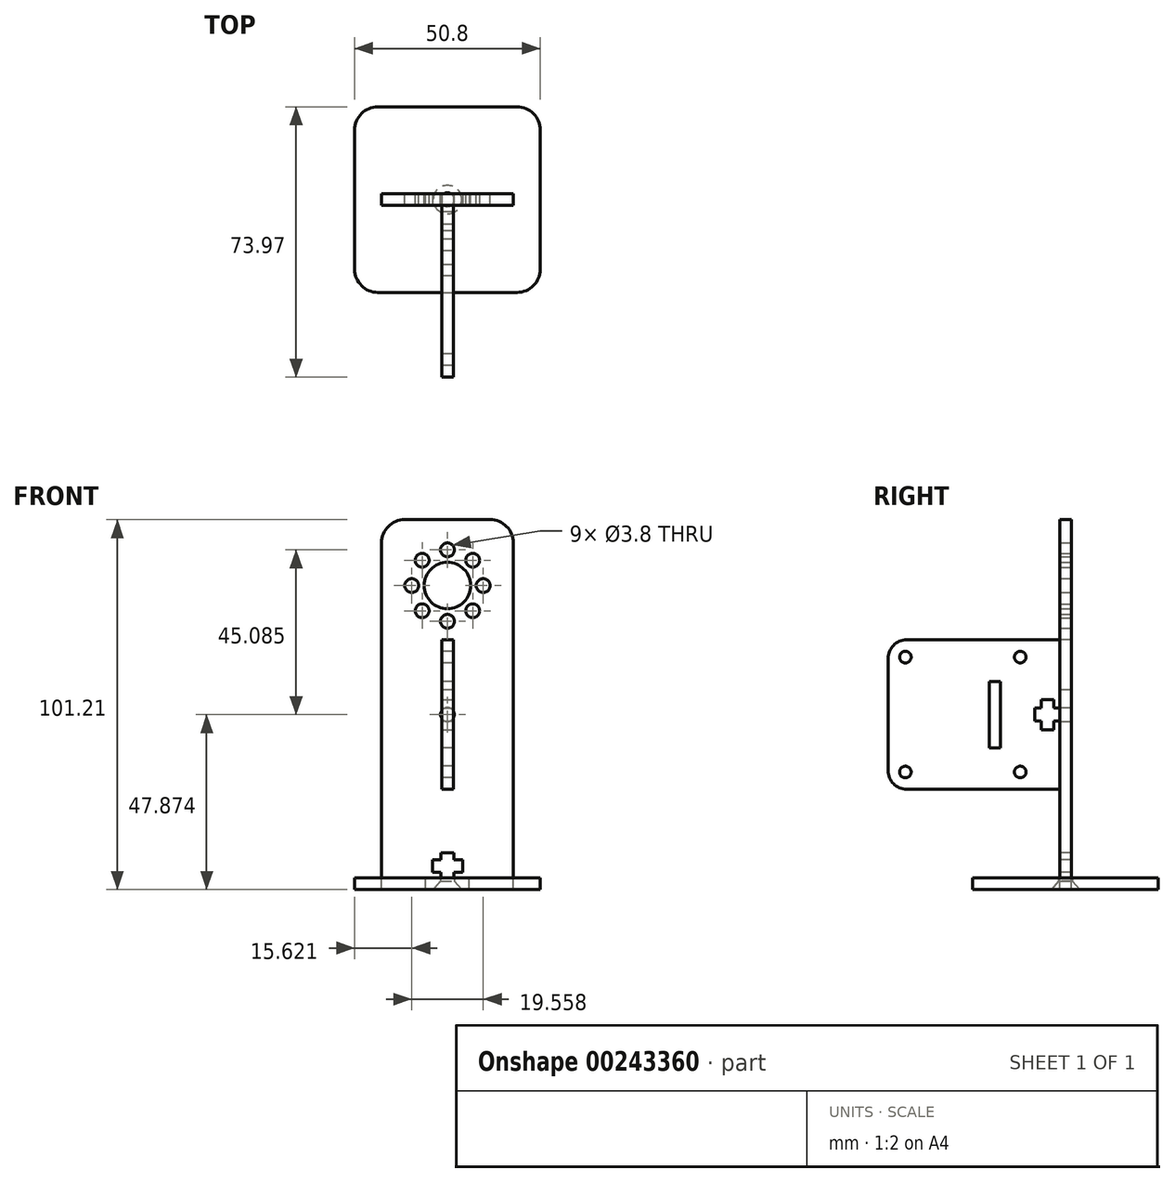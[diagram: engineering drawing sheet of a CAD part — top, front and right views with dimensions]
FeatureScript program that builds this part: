
annotation { "Feature Type Name" : "Feature", "Feature Type Description" : "" }
export const myFeature = defineFeature(function(context is Context, id is Id, definition is map)
    precondition{}
    {
        {
            var Q0;
            Q0=qCreatedBy(makeId("Front.planeOp"),FACE);
            var sketch = newSketch(context, id + "F0", { "sketchPlane" : qUnion([Q0])});
            skCircle(sketch, "E0", {"center": v(0, 0) * mm, "radius": 6.35 * mm});
            skCircle(sketch, "E1", {"center": v(0, 0) * mm, "radius": 9.78 * mm, "construction": true});
            skLineSegment(sketch, "E2", {"start": v(-6.91, 6.91) * mm, "end": v(6.91, -6.91) * mm, "construction": true});
            skLineSegment(sketch, "E3", {"start": v(-6.91, -6.91) * mm, "end": v(6.91, 6.91) * mm, "construction": true});
            skCircle(sketch, "E4", {"center": v(0, 9.78) * mm, "radius": 1.9 * mm});
            skCircle(sketch, "E5", {"center": v(6.91, 6.91) * mm, "radius": 1.9 * mm});
            skCircle(sketch, "E6", {"center": v(9.78, 0) * mm, "radius": 1.9 * mm});
            skCircle(sketch, "E7", {"center": v(6.91, -6.91) * mm, "radius": 1.9 * mm});
            skCircle(sketch, "E8", {"center": v(-6.91, -6.91) * mm, "radius": 1.9 * mm});
            skCircle(sketch, "E9", {"center": v(-6.91, 6.91) * mm, "radius": 1.9 * mm});
            skCircle(sketch, "E10", {"center": v(-9.78, 0) * mm, "radius": 1.9 * mm});
            skCircle(sketch, "E11", {"center": v(0, -9.78) * mm, "radius": 1.9 * mm});
            skLineSegment(sketch, "E12.bottom", {"start": v(-18.03, 18.03) * mm, "end": v(18.03, 18.03) * mm});
            skLineSegment(sketch, "E12.top", {"start": v(-18.03, -80) * mm, "end": v(18.03, -80) * mm});
            skLineSegment(sketch, "E12.left", {"start": v(-18.03, 18.03) * mm, "end": v(-18.03, -80) * mm});
            skLineSegment(sketch, "E12.right", {"start": v(18.03, 18.03) * mm, "end": v(18.03, -80) * mm});
            skPoint(sketch, "E13", {"position": v(0, 18.03) * mm});
            skSolve(sketch);
        }
        {
            var Q0;
            Q0 = qSketchRegion(id + "F0", true);
            extrude(context, id + "F1", {"entities" : qUnion([Q0]), "depth" : 3.17 * mm});
        }
        {
            var Q0;
            Q0=makeQuery(id+"F1.opExtrude","SWEPT_FACE",FACE,{"disambiguationData":[OSD([sQuery(id+"F0.wireOp",EDGE,"E12.top")])]});
            var sketch = newSketch(context, id + "F2", { "sketchPlane" : qUnion([Q0])});
            skLineSegment(sketch, "E14", {"start": v(-18.03, 3.18) * mm, "end": v(18.03, 0) * mm, "construction": true});
            skLineSegment(sketch, "E15.bottom", {"start": v(-25.4, 26.99) * mm, "end": v(25.4, 26.99) * mm});
            skLineSegment(sketch, "E15.top", {"start": v(-25.4, -23.81) * mm, "end": v(25.4, -23.81) * mm});
            skLineSegment(sketch, "E15.left", {"start": v(-25.4, 26.99) * mm, "end": v(-25.4, -23.81) * mm});
            skLineSegment(sketch, "E15.right", {"start": v(25.4, 26.99) * mm, "end": v(25.4, -23.81) * mm});
            skPoint(sketch, "E15.middle", {"position": v(0, 1.59) * mm});
            skSolve(sketch);
        }
        {
            var Q0;
            Q0 = qSketchRegion(id + "F2", true);
            extrude(context, id + "F3", {"entities" : qUnion([Q0]), "depth" : 3.17 * mm});
        }
        {
            var Q0;
            Q0=makeQuery(id+"F1.opExtrude","SWEPT_FACE",FACE,{"disambiguationData":[OSD([sQuery(id+"F0.wireOp",EDGE,"E12.top")])]});
            var sketch = newSketch(context, id + "F4", { "sketchPlane" : qUnion([Q0])});
            skLineSegment(sketch, "E16.bottom", {"start": v(-18.03, 3.18) * mm, "end": v(-6, 3.18) * mm});
            skLineSegment(sketch, "E16.top", {"start": v(-18.03, 0) * mm, "end": v(-6, 0) * mm});
            skLineSegment(sketch, "E16.left", {"start": v(-18.03, 3.18) * mm, "end": v(-18.03, 0) * mm});
            skLineSegment(sketch, "E16.right", {"start": v(-6, 3.18) * mm, "end": v(-6, 0) * mm});
            skLineSegment(sketch, "E17.bottom", {"start": v(-6, 0) * mm, "end": v(6, 0) * mm});
            skLineSegment(sketch, "E17.top", {"start": v(-6, 3.18) * mm, "end": v(6, 3.18) * mm});
            skLineSegment(sketch, "E17.left", {"start": v(-6, 0) * mm, "end": v(-6, 3.18) * mm});
            skLineSegment(sketch, "E17.right", {"start": v(6, 0) * mm, "end": v(6, 3.18) * mm});
            skLineSegment(sketch, "E18.bottom", {"start": v(6, 3.18) * mm, "end": v(18.03, 3.18) * mm});
            skLineSegment(sketch, "E18.top", {"start": v(6, 0) * mm, "end": v(18.03, 0) * mm});
            skLineSegment(sketch, "E18.left", {"start": v(6, 3.18) * mm, "end": v(6, 0) * mm});
            skLineSegment(sketch, "E18.right", {"start": v(18.03, 3.18) * mm, "end": v(18.03, 0) * mm});
            skSolve(sketch);
        }
        {
            var Q0;
            Q0=makeQuery(id+"F4.imprint","IMPRINT",FACE,{"disambiguationData":[TD([[makeQuery(id+"F4.imprint","IMPRINT",EDGE,{"derivedFrom":sQuery(id+"F4.wireOp",EDGE,"E16.bottom")}),-1.0]])]});
            var Q1;
            Q1=makeQuery(id+"F4.imprint","IMPRINT",FACE,{"disambiguationData":[TD([[makeQuery(id+"F4.imprint","IMPRINT",EDGE,{"derivedFrom":sQuery(id+"F4.wireOp",EDGE,"E18.bottom")}),-1.0]])]});
            extrude(context, id + "F5", {"entities" : qUnion([Q0, Q1]), "depth" : 3.17 * mm});
        }
        {
            var Q0;
            Q0=makeQuery(id+"F5.opExtrude","SWEPT_BODY",BODY,{"disambiguationData":[OSD([sQuery(id+"F4.wireOp",EDGE,"E18.bottom"),sQuery(id+"F4.wireOp",EDGE,"E18.top"),sQuery(id+"F4.wireOp",EDGE,"E18.left"),sQuery(id+"F4.wireOp",EDGE,"E18.right")])]});
            var Q1;
            Q1=makeQuery(id+"F5.opExtrude","SWEPT_BODY",BODY,{"disambiguationData":[OSD([sQuery(id+"F4.wireOp",EDGE,"E16.bottom"),sQuery(id+"F4.wireOp",EDGE,"E16.top"),sQuery(id+"F4.wireOp",EDGE,"E16.left"),sQuery(id+"F4.wireOp",EDGE,"E17.left")])]});
            var Q2;
            Q2=makeQuery(id+"F3.opExtrude","SWEPT_BODY",BODY,{"disambiguationData":[OSD([sQuery(id+"F2.wireOp",EDGE,"E15.bottom"),sQuery(id+"F2.wireOp",EDGE,"E15.top"),sQuery(id+"F2.wireOp",EDGE,"E15.left"),sQuery(id+"F2.wireOp",EDGE,"E15.right")])]});
            booleanBodies(context, id + "F6", {"operationType" : BooleanOperationType.SUBTRACTION, "tools" : qUnion([Q0, Q1]), "targets" : qUnion([Q2]), "keepTools" : true});
        }
        {
            var Q0;
            Q0=makeQuery(id+"F5.opExtrude","SWEPT_BODY",BODY,{"disambiguationData":[OSD([sQuery(id+"F4.wireOp",EDGE,"E16.bottom"),sQuery(id+"F4.wireOp",EDGE,"E16.top"),sQuery(id+"F4.wireOp",EDGE,"E16.left"),sQuery(id+"F4.wireOp",EDGE,"E17.left")])]});
            var Q1;
            Q1=makeQuery(id+"F5.opExtrude","SWEPT_BODY",BODY,{"disambiguationData":[OSD([sQuery(id+"F4.wireOp",EDGE,"E18.bottom"),sQuery(id+"F4.wireOp",EDGE,"E18.top"),sQuery(id+"F4.wireOp",EDGE,"E18.left"),sQuery(id+"F4.wireOp",EDGE,"E18.right")])]});
            var Q2;
            Q2=makeQuery(id+"F1.opExtrude","SWEPT_BODY",BODY,{"disambiguationData":[OSD([sQuery(id+"F0.wireOp",EDGE,"E0"),sQuery(id+"F0.wireOp",EDGE,"E4"),sQuery(id+"F0.wireOp",EDGE,"E5"),sQuery(id+"F0.wireOp",EDGE,"E6"),sQuery(id+"F0.wireOp",EDGE,"E7"),sQuery(id+"F0.wireOp",EDGE,"E8"),sQuery(id+"F0.wireOp",EDGE,"E9"),sQuery(id+"F0.wireOp",EDGE,"E10"),sQuery(id+"F0.wireOp",EDGE,"E11"),sQuery(id+"F0.wireOp",EDGE,"E12.bottom"),sQuery(id+"F0.wireOp",EDGE,"E12.top"),sQuery(id+"F0.wireOp",EDGE,"E12.left"),sQuery(id+"F0.wireOp",EDGE,"E12.right")])]});
            booleanBodies(context, id + "F7", {"operationType" : BooleanOperationType.UNION, "tools" : qUnion([Q0, Q1, Q2])});
        }
        {
            var Q0;
            Q0=makeQuery(id+"F3.opExtrude","CAP_FACE",FACE,{"disambiguationData":[OSD([sQuery(id+"F2.wireOp",EDGE,"E15.bottom"),sQuery(id+"F2.wireOp",EDGE,"E15.top"),sQuery(id+"F2.wireOp",EDGE,"E15.left"),sQuery(id+"F2.wireOp",EDGE,"E15.right")])],"isStart":false});
            var sketch = newSketch(context, id + "F8", { "sketchPlane" : qUnion([Q0])});
            skLineSegment(sketch, "E19", {"start": v(-6, 3.17) * mm, "end": v(6, 0) * mm, "construction": true});
            skCircle(sketch, "E20", {"center": v(0, 1.59) * mm, "radius": 1.9 * mm});
            skSolve(sketch);
        }
        {
            var Q0;
            Q0 = qSketchRegion(id + "F8", true);
            var Q1;
            Q1=makeQuery(id+"F3.opExtrude","CAP_FACE",FACE,{"disambiguationData":[OSD([sQuery(id+"F2.wireOp",EDGE,"E15.bottom"),sQuery(id+"F2.wireOp",EDGE,"E15.top"),sQuery(id+"F2.wireOp",EDGE,"E15.left"),sQuery(id+"F2.wireOp",EDGE,"E15.right")])],"isStart":true});
            extrude(context, id + "F9", {"entities" : qUnion([Q0]), "operationType" : NewBodyOperationType.REMOVE, "endBound" : BoundingType.UP_TO_SURFACE, "oppositeDirection" : true, "endBoundEntityFace" : qUnion([Q1]), "depth" : 25.4 * mm});
        }
        {
            var Q0;
            Q0=makeQuery(id+"F7.opBoolean","MERGE",FACE,{"derivedFrom":[makeQuery(id+"F1.opExtrude","CAP_FACE",FACE,{"disambiguationData":[OSD([sQuery(id+"F0.wireOp",EDGE,"E0"),sQuery(id+"F0.wireOp",EDGE,"E4"),sQuery(id+"F0.wireOp",EDGE,"E5"),sQuery(id+"F0.wireOp",EDGE,"E6"),sQuery(id+"F0.wireOp",EDGE,"E7"),sQuery(id+"F0.wireOp",EDGE,"E8"),sQuery(id+"F0.wireOp",EDGE,"E9"),sQuery(id+"F0.wireOp",EDGE,"E10"),sQuery(id+"F0.wireOp",EDGE,"E11"),sQuery(id+"F0.wireOp",EDGE,"E12.bottom"),sQuery(id+"F0.wireOp",EDGE,"E12.top"),sQuery(id+"F0.wireOp",EDGE,"E12.left"),sQuery(id+"F0.wireOp",EDGE,"E12.right")])],"isStart":false}),makeQuery(id+"F5.opExtrude","SWEPT_FACE",FACE,{"disambiguationData":[OSD([sQuery(id+"F4.wireOp",EDGE,"E16.bottom")])]}),makeQuery(id+"F5.opExtrude","SWEPT_FACE",FACE,{"disambiguationData":[OSD([sQuery(id+"F4.wireOp",EDGE,"E18.bottom")])]})]});
            var sketch = newSketch(context, id + "F10", { "sketchPlane" : qUnion([Q0])});
            skLineSegment(sketch, "E21", {"start": v(0, -80) * mm, "end": v(0, -73.14) * mm, "construction": true});
            skPoint(sketch, "E21.endSnap0", {"position": v(0, -80) * mm});
            skLineSegment(sketch, "E22", {"start": v(0, -73.14) * mm, "end": v(-1.78, -73.14) * mm});
            skLineSegment(sketch, "E23", {"start": v(-1.78, -73.14) * mm, "end": v(-1.78, -74.97) * mm});
            skLineSegment(sketch, "E24", {"start": v(-1.78, -74.97) * mm, "end": v(-4.13, -74.97) * mm});
            skLineSegment(sketch, "E25", {"start": v(-4.13, -74.97) * mm, "end": v(-4.13, -78.4) * mm});
            skLineSegment(sketch, "E26", {"start": v(-4.13, -78.4) * mm, "end": v(-1.78, -78.4) * mm});
            skLineSegment(sketch, "E27", {"start": v(-1.78, -78.4) * mm, "end": v(-1.78, -80) * mm});
            skLineSegment(sketch, "E28", {"start": v(-1.78, -80) * mm, "end": v(0, -80) * mm});
            skLineSegment(sketch, "E29.MirrorCS", {"start": v(0, -73.14) * mm, "end": v(1.78, -73.14) * mm});
            skLineSegment(sketch, "E30.MirrorCS", {"start": v(1.78, -73.14) * mm, "end": v(1.78, -74.97) * mm});
            skLineSegment(sketch, "E31.MirrorCS", {"start": v(1.78, -74.97) * mm, "end": v(4.13, -74.97) * mm});
            skLineSegment(sketch, "E32.MirrorCS", {"start": v(4.13, -74.97) * mm, "end": v(4.13, -78.4) * mm});
            skLineSegment(sketch, "E33.MirrorCS", {"start": v(4.13, -78.4) * mm, "end": v(1.78, -78.4) * mm});
            skLineSegment(sketch, "E34.MirrorCS", {"start": v(1.78, -78.4) * mm, "end": v(1.78, -80) * mm});
            skLineSegment(sketch, "E35.MirrorCS", {"start": v(1.78, -80) * mm, "end": v(0, -80) * mm});
            skSolve(sketch);
        }
        {
            var Q0;
            Q0 = qSketchRegion(id + "F10", true);
            var Q1;
            Q1=makeQuery(id+"F7.opBoolean","MERGE",FACE,{"derivedFrom":[makeQuery(id+"F1.opExtrude","CAP_FACE",FACE,{"disambiguationData":[OSD([sQuery(id+"F0.wireOp",EDGE,"E0"),sQuery(id+"F0.wireOp",EDGE,"E4"),sQuery(id+"F0.wireOp",EDGE,"E5"),sQuery(id+"F0.wireOp",EDGE,"E6"),sQuery(id+"F0.wireOp",EDGE,"E7"),sQuery(id+"F0.wireOp",EDGE,"E8"),sQuery(id+"F0.wireOp",EDGE,"E9"),sQuery(id+"F0.wireOp",EDGE,"E10"),sQuery(id+"F0.wireOp",EDGE,"E11"),sQuery(id+"F0.wireOp",EDGE,"E12.bottom"),sQuery(id+"F0.wireOp",EDGE,"E12.top"),sQuery(id+"F0.wireOp",EDGE,"E12.left"),sQuery(id+"F0.wireOp",EDGE,"E12.right")])],"isStart":true}),makeQuery(id+"F5.opExtrude","SWEPT_FACE",FACE,{"disambiguationData":[OSD([sQuery(id+"F4.wireOp",EDGE,"E16.top")])]}),makeQuery(id+"F5.opExtrude","SWEPT_FACE",FACE,{"disambiguationData":[OSD([sQuery(id+"F4.wireOp",EDGE,"E18.top")])]})]});
            extrude(context, id + "F11", {"entities" : qUnion([Q0]), "operationType" : NewBodyOperationType.REMOVE, "endBound" : BoundingType.UP_TO_SURFACE, "oppositeDirection" : true, "endBoundEntityFace" : qUnion([Q1]), "depth" : 25.4 * mm});
        }
        {
            var Q0;
            Q0=sQuery(id+"F8.wireOp",VERTEX,"E20.center");
            var Q1;
            Q1=makeQuery(id+"F3.opExtrude","SWEPT_BODY",BODY,{"disambiguationData":[OSD([sQuery(id+"F2.wireOp",EDGE,"E15.bottom"),sQuery(id+"F2.wireOp",EDGE,"E15.top"),sQuery(id+"F2.wireOp",EDGE,"E15.left"),sQuery(id+"F2.wireOp",EDGE,"E15.right")])]});
            hole(context, id + "F12", {"style" : HoleStyle.C_SINK, "endStyle" : HoleEndStyle.THROUGH, "holeDiameter" : 3.8 * mm, "cSinkDiameter" : 7.8 * mm, "cSinkAngle" : 82 * degree, "tappedDepth" : 12.7 * mm, "tapClearance" : 3, "locations" : qUnion([Q0]), "scope" : qUnion([Q1])});
        }
        {
            var Q0;
            Q0=makeQuery(id+"F3.opExtrude","SWEPT_EDGE",EDGE,{"disambiguationData":[OSD([sQuery(id+"F2.wireOp",EDGE,"E15.bottom"),sQuery(id+"F2.wireOp",EDGE,"E15.left")])]});
            var Q1;
            Q1=makeQuery(id+"F3.opExtrude","SWEPT_EDGE",EDGE,{"disambiguationData":[OSD([sQuery(id+"F2.wireOp",EDGE,"E15.top"),sQuery(id+"F2.wireOp",EDGE,"E15.left")])]});
            var Q2;
            Q2=makeQuery(id+"F3.opExtrude","SWEPT_EDGE",EDGE,{"disambiguationData":[OSD([sQuery(id+"F2.wireOp",EDGE,"E15.top"),sQuery(id+"F2.wireOp",EDGE,"E15.right")])]});
            var Q3;
            Q3=makeQuery(id+"F3.opExtrude","SWEPT_EDGE",EDGE,{"disambiguationData":[OSD([sQuery(id+"F2.wireOp",EDGE,"E15.bottom"),sQuery(id+"F2.wireOp",EDGE,"E15.right")])]});
            var Q4;
            Q4=makeQuery(id+"F1.opExtrude","SWEPT_EDGE",EDGE,{"disambiguationData":[OSD([sQuery(id+"F0.wireOp",EDGE,"E12.bottom"),sQuery(id+"F0.wireOp",EDGE,"E12.right")])]});
            var Q5;
            Q5=makeQuery(id+"F1.opExtrude","SWEPT_EDGE",EDGE,{"disambiguationData":[OSD([sQuery(id+"F0.wireOp",EDGE,"E12.bottom"),sQuery(id+"F0.wireOp",EDGE,"E12.left")])]});
            fillet(context, id + "F13", {"entities" : qUnion([Q0, Q1, Q2, Q3, Q4, Q5]), "radius" : 6.35 * mm, "tangentPropagation" : true, "allowEdgeOverflow" : false});
        }
        {
            var Q0;
            Q0=makeQuery(id+"F7.opBoolean","MERGE",FACE,{"derivedFrom":[makeQuery(id+"F1.opExtrude","CAP_FACE",FACE,{"disambiguationData":[OSD([sQuery(id+"F0.wireOp",EDGE,"E0"),sQuery(id+"F0.wireOp",EDGE,"E4"),sQuery(id+"F0.wireOp",EDGE,"E5"),sQuery(id+"F0.wireOp",EDGE,"E6"),sQuery(id+"F0.wireOp",EDGE,"E7"),sQuery(id+"F0.wireOp",EDGE,"E8"),sQuery(id+"F0.wireOp",EDGE,"E9"),sQuery(id+"F0.wireOp",EDGE,"E10"),sQuery(id+"F0.wireOp",EDGE,"E11"),sQuery(id+"F0.wireOp",EDGE,"E12.bottom"),sQuery(id+"F0.wireOp",EDGE,"E12.top"),sQuery(id+"F0.wireOp",EDGE,"E12.left"),sQuery(id+"F0.wireOp",EDGE,"E12.right")])],"isStart":false}),makeQuery(id+"F5.opExtrude","SWEPT_FACE",FACE,{"disambiguationData":[OSD([sQuery(id+"F4.wireOp",EDGE,"E16.bottom")])]}),makeQuery(id+"F5.opExtrude","SWEPT_FACE",FACE,{"disambiguationData":[OSD([sQuery(id+"F4.wireOp",EDGE,"E18.bottom")])]})]});
            var sketch = newSketch(context, id + "F14", { "sketchPlane" : qUnion([Q0])});
            skLineSegment(sketch, "E36.bottom", {"start": v(1.59, -55.76) * mm, "end": v(-1.59, -55.76) * mm});
            skLineSegment(sketch, "E36.top", {"start": v(1.59, -14.85) * mm, "end": v(-1.59, -14.85) * mm});
            skLineSegment(sketch, "E36.left", {"start": v(1.59, -55.76) * mm, "end": v(1.59, -14.85) * mm});
            skLineSegment(sketch, "E36.right", {"start": v(-1.59, -55.76) * mm, "end": v(-1.59, -14.85) * mm});
            skPoint(sketch, "E36.middle", {"position": v(0, -35.3) * mm});
            skSolve(sketch);
        }
        {
            var Q0;
            Q0 = qSketchRegion(id + "F14", true);
            extrude(context, id + "F15", {"entities" : qUnion([Q0]), "depth" : 47 * mm});
        }
        {
            var Q0;
            Q0=makeQuery(id+"F15.opExtrude","SWEPT_FACE",FACE,{"disambiguationData":[OSD([sQuery(id+"F14.wireOp",EDGE,"E36.right")])]});
            var sketch = newSketch(context, id + "F16", { "sketchPlane" : qUnion([Q0])});
            skCircle(sketch, "E37", {"center": v(14, -19.59) * mm, "radius": 1.59 * mm});
            skCircle(sketch, "E38", {"center": v(14, -51.02) * mm, "radius": 1.59 * mm});
            skCircle(sketch, "E39", {"center": v(45.43, -51.02) * mm, "radius": 1.59 * mm});
            skCircle(sketch, "E40", {"center": v(45.43, -19.59) * mm, "radius": 1.59 * mm});
            skLineSegment(sketch, "E41", {"start": v(3.18, -35.3) * mm, "end": v(50.16, -35.3) * mm, "construction": true});
            skLineSegment(sketch, "E42", {"start": v(45.43, -19.59) * mm, "end": v(45.43, -51.02) * mm, "construction": true});
            skPoint(sketch, "E43", {"position": v(45.43, -35.3) * mm});
            skLineSegment(sketch, "E44", {"start": v(45.43, -19.59) * mm, "end": v(14, -19.59) * mm, "construction": true});
            skLineSegment(sketch, "E45.bottom", {"start": v(22.48, -26.21) * mm, "end": v(19.43, -26.21) * mm});
            skLineSegment(sketch, "E45.top", {"start": v(22.48, -44.4) * mm, "end": v(19.43, -44.4) * mm});
            skLineSegment(sketch, "E45.left", {"start": v(22.48, -26.21) * mm, "end": v(22.48, -44.4) * mm});
            skLineSegment(sketch, "E45.right", {"start": v(19.43, -26.21) * mm, "end": v(19.43, -44.4) * mm});
            skPoint(sketch, "E45.middle", {"position": v(20.95, -35.3) * mm});
            skLineSegment(sketch, "E46", {"start": v(45.43, -19.59) * mm, "end": v(45.43, -14.85) * mm, "construction": true});
            skLineSegment(sketch, "E47", {"start": v(45.43, -19.59) * mm, "end": v(50.16, -19.59) * mm, "construction": true});
            skSolve(sketch);
        }
        {
            var Q0;
            Q0 = qSketchRegion(id + "F16", true);
            var Q1;
            Q1=makeQuery(id+"F15.opExtrude","SWEPT_FACE",FACE,{"disambiguationData":[OSD([sQuery(id+"F14.wireOp",EDGE,"E36.left")])]});
            extrude(context, id + "F17", {"entities" : qUnion([Q0]), "operationType" : NewBodyOperationType.REMOVE, "endBound" : BoundingType.UP_TO_SURFACE, "oppositeDirection" : true, "endBoundEntityFace" : qUnion([Q1]), "depth" : 25.4 * mm});
        }
        {
            var Q0;
            Q0=makeQuery(id+"F15.opExtrude","CAP_FACE",FACE,{"disambiguationData":[OSD([sQuery(id+"F14.wireOp",EDGE,"E36.bottom"),sQuery(id+"F14.wireOp",EDGE,"E36.top"),sQuery(id+"F14.wireOp",EDGE,"E36.left"),sQuery(id+"F14.wireOp",EDGE,"E36.right")])],"isStart":true});
            var sketch = newSketch(context, id + "F18", { "sketchPlane" : qUnion([Q0])});
            skLineSegment(sketch, "E48.bottom", {"start": v(-1.59, -14.85) * mm, "end": v(1.59, -14.85) * mm});
            skLineSegment(sketch, "E48.top", {"start": v(-1.59, -28.49) * mm, "end": v(1.59, -28.49) * mm});
            skLineSegment(sketch, "E48.left", {"start": v(-1.59, -14.85) * mm, "end": v(-1.59, -28.49) * mm});
            skLineSegment(sketch, "E48.right", {"start": v(1.59, -14.85) * mm, "end": v(1.59, -28.49) * mm});
            skLineSegment(sketch, "E49.bottom", {"start": v(1.59, -28.49) * mm, "end": v(-1.59, -28.49) * mm});
            skLineSegment(sketch, "E49.top", {"start": v(1.59, -42.12) * mm, "end": v(-1.59, -42.12) * mm});
            skLineSegment(sketch, "E49.left", {"start": v(1.59, -28.49) * mm, "end": v(1.59, -42.12) * mm});
            skLineSegment(sketch, "E49.right", {"start": v(-1.59, -28.49) * mm, "end": v(-1.59, -42.12) * mm});
            skLineSegment(sketch, "E50.bottom", {"start": v(-1.59, -42.12) * mm, "end": v(1.59, -42.12) * mm});
            skLineSegment(sketch, "E50.top", {"start": v(-1.59, -55.76) * mm, "end": v(1.59, -55.76) * mm});
            skLineSegment(sketch, "E50.left", {"start": v(-1.59, -42.12) * mm, "end": v(-1.59, -55.76) * mm});
            skLineSegment(sketch, "E50.right", {"start": v(1.59, -42.12) * mm, "end": v(1.59, -55.76) * mm});
            skSolve(sketch);
        }
        {
            var Q0;
            Q0=makeQuery(id+"F18.imprint","IMPRINT",FACE,{"disambiguationData":[TD([[makeQuery(id+"F18.imprint","IMPRINT",EDGE,{"derivedFrom":sQuery(id+"F18.wireOp",EDGE,"E48.bottom")}),-1.0]])]});
            var Q1;
            Q1=makeQuery(id+"F18.imprint","IMPRINT",FACE,{"disambiguationData":[TD([[makeQuery(id+"F18.imprint","IMPRINT",EDGE,{"derivedFrom":sQuery(id+"F18.wireOp",EDGE,"E50.bottom")}),-1.0]])]});
            extrude(context, id + "F19", {"entities" : qUnion([Q0, Q1]), "depth" : 3.17 * mm});
        }
        {
            var Q0;
            Q0=makeQuery(id+"F19.opExtrude","SWEPT_BODY",BODY,{"disambiguationData":[OSD([sQuery(id+"F18.wireOp",EDGE,"E50.bottom"),sQuery(id+"F18.wireOp",EDGE,"E50.top"),sQuery(id+"F18.wireOp",EDGE,"E50.left"),sQuery(id+"F18.wireOp",EDGE,"E50.right")])]});
            var Q1;
            Q1=makeQuery(id+"F19.opExtrude","SWEPT_BODY",BODY,{"disambiguationData":[OSD([sQuery(id+"F18.wireOp",EDGE,"E48.bottom"),sQuery(id+"F18.wireOp",EDGE,"E48.left"),sQuery(id+"F18.wireOp",EDGE,"E48.right"),sQuery(id+"F18.wireOp",EDGE,"E49.bottom")])]});
            var Q2;
            Q2=makeQuery(id+"F5.opExtrude","SWEPT_BODY",BODY,{"disambiguationData":[OSD([sQuery(id+"F4.wireOp",EDGE,"E16.bottom"),sQuery(id+"F4.wireOp",EDGE,"E16.top"),sQuery(id+"F4.wireOp",EDGE,"E16.left"),sQuery(id+"F4.wireOp",EDGE,"E17.left")])]});
            booleanBodies(context, id + "F20", {"operationType" : BooleanOperationType.SUBTRACTION, "tools" : qUnion([Q0, Q1]), "targets" : qUnion([Q2]), "keepTools" : true});
        }
        {
            var Q0;
            Q0=makeQuery(id+"F19.opExtrude","SWEPT_BODY",BODY,{"disambiguationData":[OSD([sQuery(id+"F18.wireOp",EDGE,"E50.bottom"),sQuery(id+"F18.wireOp",EDGE,"E50.top"),sQuery(id+"F18.wireOp",EDGE,"E50.left"),sQuery(id+"F18.wireOp",EDGE,"E50.right")])]});
            var Q1;
            Q1=makeQuery(id+"F19.opExtrude","SWEPT_BODY",BODY,{"disambiguationData":[OSD([sQuery(id+"F18.wireOp",EDGE,"E48.bottom"),sQuery(id+"F18.wireOp",EDGE,"E48.left"),sQuery(id+"F18.wireOp",EDGE,"E48.right"),sQuery(id+"F18.wireOp",EDGE,"E49.bottom")])]});
            var Q2;
            Q2=makeQuery(id+"F15.opExtrude","SWEPT_BODY",BODY,{"disambiguationData":[OSD([sQuery(id+"F14.wireOp",EDGE,"E36.bottom"),sQuery(id+"F14.wireOp",EDGE,"E36.top"),sQuery(id+"F14.wireOp",EDGE,"E36.left"),sQuery(id+"F14.wireOp",EDGE,"E36.right")])]});
            booleanBodies(context, id + "F21", {"operationType" : BooleanOperationType.UNION, "tools" : qUnion([Q0, Q1, Q2])});
        }
        {
            var Q0;
            Q0=makeQuery(id+"F7.opBoolean","MERGE",FACE,{"derivedFrom":[makeQuery(id+"F1.opExtrude","CAP_FACE",FACE,{"disambiguationData":[OSD([sQuery(id+"F0.wireOp",EDGE,"E0"),sQuery(id+"F0.wireOp",EDGE,"E4"),sQuery(id+"F0.wireOp",EDGE,"E5"),sQuery(id+"F0.wireOp",EDGE,"E6"),sQuery(id+"F0.wireOp",EDGE,"E7"),sQuery(id+"F0.wireOp",EDGE,"E8"),sQuery(id+"F0.wireOp",EDGE,"E9"),sQuery(id+"F0.wireOp",EDGE,"E10"),sQuery(id+"F0.wireOp",EDGE,"E11"),sQuery(id+"F0.wireOp",EDGE,"E12.bottom"),sQuery(id+"F0.wireOp",EDGE,"E12.top"),sQuery(id+"F0.wireOp",EDGE,"E12.left"),sQuery(id+"F0.wireOp",EDGE,"E12.right")])],"isStart":true}),makeQuery(id+"F5.opExtrude","SWEPT_FACE",FACE,{"disambiguationData":[OSD([sQuery(id+"F4.wireOp",EDGE,"E16.top")])]}),makeQuery(id+"F5.opExtrude","SWEPT_FACE",FACE,{"disambiguationData":[OSD([sQuery(id+"F4.wireOp",EDGE,"E18.top")])]})]});
            var sketch = newSketch(context, id + "F22", { "sketchPlane" : qUnion([Q0])});
            skLineSegment(sketch, "E51", {"start": v(1.59, -28.49) * mm, "end": v(-1.59, -42.12) * mm, "construction": true});
            skCircle(sketch, "E52", {"center": v(0, -35.3) * mm, "radius": 1.9 * mm});
            skSolve(sketch);
        }
        {
            var Q0;
            Q0 = qSketchRegion(id + "F22", true);
            var Q1;
            Q1=makeQuery(id+"F7.opBoolean","MERGE",FACE,{"derivedFrom":[makeQuery(id+"F1.opExtrude","CAP_FACE",FACE,{"disambiguationData":[OSD([sQuery(id+"F0.wireOp",EDGE,"E0"),sQuery(id+"F0.wireOp",EDGE,"E4"),sQuery(id+"F0.wireOp",EDGE,"E5"),sQuery(id+"F0.wireOp",EDGE,"E6"),sQuery(id+"F0.wireOp",EDGE,"E7"),sQuery(id+"F0.wireOp",EDGE,"E8"),sQuery(id+"F0.wireOp",EDGE,"E9"),sQuery(id+"F0.wireOp",EDGE,"E10"),sQuery(id+"F0.wireOp",EDGE,"E11"),sQuery(id+"F0.wireOp",EDGE,"E12.bottom"),sQuery(id+"F0.wireOp",EDGE,"E12.top"),sQuery(id+"F0.wireOp",EDGE,"E12.left"),sQuery(id+"F0.wireOp",EDGE,"E12.right")])],"isStart":false}),makeQuery(id+"F5.opExtrude","SWEPT_FACE",FACE,{"disambiguationData":[OSD([sQuery(id+"F4.wireOp",EDGE,"E16.bottom")])]}),makeQuery(id+"F5.opExtrude","SWEPT_FACE",FACE,{"disambiguationData":[OSD([sQuery(id+"F4.wireOp",EDGE,"E18.bottom")])]})]});
            extrude(context, id + "F23", {"entities" : qUnion([Q0]), "operationType" : NewBodyOperationType.REMOVE, "endBound" : BoundingType.UP_TO_SURFACE, "oppositeDirection" : true, "endBoundEntityFace" : qUnion([Q1]), "depth" : 25.4 * mm});
        }
        {
            var Q0;
            Q0=makeQuery(id+"F21.opBoolean","MERGE",FACE,{"derivedFrom":[makeQuery(id+"F15.opExtrude","SWEPT_FACE",FACE,{"disambiguationData":[OSD([sQuery(id+"F14.wireOp",EDGE,"E36.left")])]}),makeQuery(id+"F19.opExtrude","SWEPT_FACE",FACE,{"disambiguationData":[OSD([sQuery(id+"F18.wireOp",EDGE,"E48.left")])]}),makeQuery(id+"F19.opExtrude","SWEPT_FACE",FACE,{"disambiguationData":[OSD([sQuery(id+"F18.wireOp",EDGE,"E50.left")])]})]});
            var sketch = newSketch(context, id + "F24", { "sketchPlane" : qUnion([Q0])});
            skLineSegment(sketch, "E53", {"start": v(-3.18, -35.3) * mm, "end": v(-10.03, -35.3) * mm, "construction": true});
            skLineSegment(sketch, "E54", {"start": v(-10.03, -35.3) * mm, "end": v(-10.03, -37.08) * mm});
            skLineSegment(sketch, "E55", {"start": v(-10.03, -37.08) * mm, "end": v(-8.2, -37.08) * mm});
            skLineSegment(sketch, "E56", {"start": v(-8.2, -37.08) * mm, "end": v(-8.2, -39.43) * mm});
            skLineSegment(sketch, "E57", {"start": v(-8.2, -39.43) * mm, "end": v(-4.78, -39.43) * mm});
            skLineSegment(sketch, "E58", {"start": v(-4.78, -39.43) * mm, "end": v(-4.78, -37.08) * mm});
            skLineSegment(sketch, "E59", {"start": v(-4.78, -37.08) * mm, "end": v(-3.18, -37.08) * mm});
            skLineSegment(sketch, "E60", {"start": v(-3.18, -37.08) * mm, "end": v(-3.18, -35.3) * mm});
            skLineSegment(sketch, "E61.MirrorCS", {"start": v(-10.03, -35.3) * mm, "end": v(-10.03, -33.53) * mm});
            skLineSegment(sketch, "E62.MirrorCS", {"start": v(-10.03, -33.53) * mm, "end": v(-8.2, -33.53) * mm});
            skLineSegment(sketch, "E63.MirrorCS", {"start": v(-8.2, -33.53) * mm, "end": v(-8.2, -31.18) * mm});
            skLineSegment(sketch, "E64.MirrorCS", {"start": v(-4.78, -31.18) * mm, "end": v(-4.78, -33.53) * mm});
            skLineSegment(sketch, "E65.MirrorCS", {"start": v(-8.2, -31.18) * mm, "end": v(-4.78, -31.18) * mm});
            skLineSegment(sketch, "E66.MirrorCS", {"start": v(-4.78, -33.53) * mm, "end": v(-3.18, -33.53) * mm});
            skLineSegment(sketch, "E67.MirrorCS", {"start": v(-3.18, -33.53) * mm, "end": v(-3.18, -35.3) * mm});
            skSolve(sketch);
        }
        {
            var Q0;
            Q0 = qSketchRegion(id + "F24", true);
            var Q1;
            Q1=makeQuery(id+"F21.opBoolean","MERGE",FACE,{"derivedFrom":[makeQuery(id+"F15.opExtrude","SWEPT_FACE",FACE,{"disambiguationData":[OSD([sQuery(id+"F14.wireOp",EDGE,"E36.right")])]}),makeQuery(id+"F19.opExtrude","SWEPT_FACE",FACE,{"disambiguationData":[OSD([sQuery(id+"F18.wireOp",EDGE,"E48.right")])]}),makeQuery(id+"F19.opExtrude","SWEPT_FACE",FACE,{"disambiguationData":[OSD([sQuery(id+"F18.wireOp",EDGE,"E50.right")])]})]});
            extrude(context, id + "F25", {"entities" : qUnion([Q0]), "operationType" : NewBodyOperationType.REMOVE, "endBound" : BoundingType.UP_TO_SURFACE, "oppositeDirection" : true, "endBoundEntityFace" : qUnion([Q1]), "depth" : 25.4 * mm});
        }
        {
            var Q0;
            Q0=makeQuery(id+"F15.opExtrude","CAP_EDGE",EDGE,{"disambiguationData":[OSD([sQuery(id+"F14.wireOp",EDGE,"E36.bottom")])],"isStart":false});
            var Q1;
            Q1=makeQuery(id+"F15.opExtrude","CAP_EDGE",EDGE,{"disambiguationData":[OSD([sQuery(id+"F14.wireOp",EDGE,"E36.top")])],"isStart":false});
            fillet(context, id + "F26", {"entities" : qUnion([Q0, Q1]), "radius" : 5.08 * mm, "tangentPropagation" : true, "allowEdgeOverflow" : false});
        }
    });
